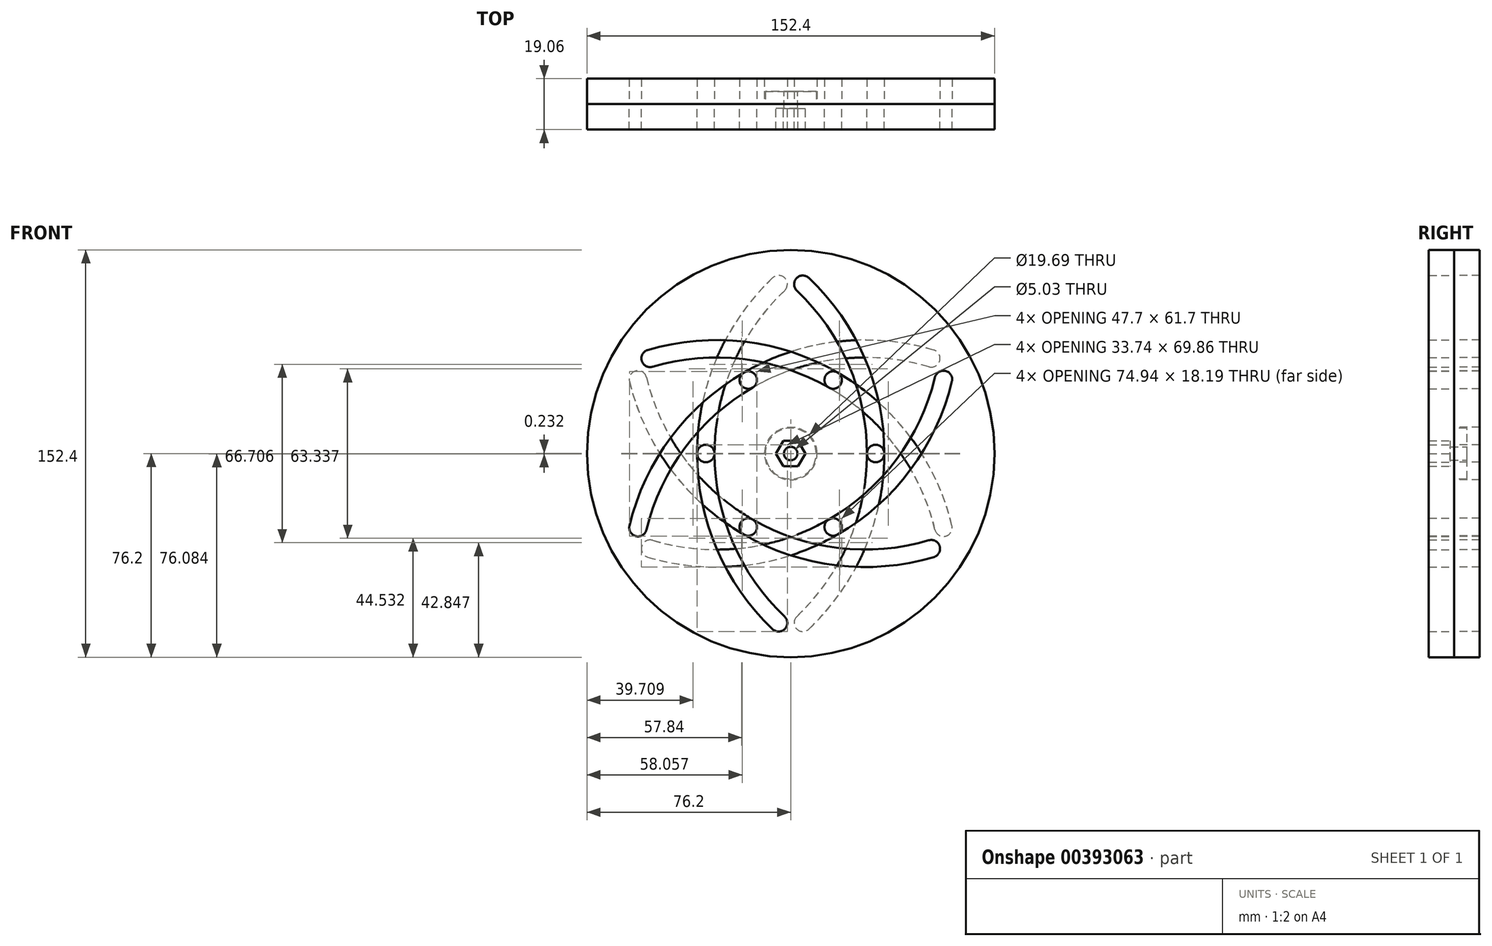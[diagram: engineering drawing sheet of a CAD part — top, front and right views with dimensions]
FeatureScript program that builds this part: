
annotation { "Feature Type Name" : "Feature", "Feature Type Description" : "" }
export const myFeature = defineFeature(function(context is Context, id is Id, definition is map)
    precondition{}
    {
        {
            var Q0;
            Q0=qCreatedBy(makeId("Front.planeOp"),FACE);
            var sketch = newSketch(context, id + "F0", { "sketchPlane" : qUnion([Q0])});
            skCircle(sketch, "E0", {"center": v(0, 0) * mm, "radius": 76.2 * mm});
            skLineSegment(sketch, "E1", {"start": v(38.1, -66) * mm, "end": v(-38.1, 66) * mm, "construction": true});
            skLineSegment(sketch, "E2", {"start": v(-76.2, 0) * mm, "end": v(76.2, 0) * mm, "construction": true});
            skCircle(sketch, "E3", {"center": v(0, 0) * mm, "radius": 63.5 * mm, "construction": true});
            skCircle(sketch, "E4", {"center": v(0, 0) * mm, "radius": 55.56 * mm, "construction": true});
            skCircle(sketch, "E5", {"center": v(0, 0) * mm, "radius": 31.75 * mm, "construction": true});
            skLineSegment(sketch, "E6", {"start": v(31.54, -3.6) * mm, "end": v(63.09, -7.22) * mm, "construction": true});
            skPoint(sketch, "E7", {"position": v(47.32, -5.41) * mm});
            skArc(sketch, "E8", {"start": v(57.12, 27.74) * mm, "mid": v(42.18, -4.12) * mm, "end": v(15.87, -27.5) * mm, "construction": true});
            skArc(sketch, "E9.0.startCap", {"start": v(53.95, 28.5) * mm, "mid": v(57.88, 30.91) * mm, "end": v(60.3, 26.98) * mm});
            skArc(sketch, "E9.0.endCap", {"start": v(17.5, -30.32) * mm, "mid": v(13.05, -29.13) * mm, "end": v(14.24, -24.67) * mm});
            skArc(sketch, "E9.0.left", {"start": v(60.3, 26.98) * mm, "mid": v(44.8, -6.07) * mm, "end": v(17.5, -30.32) * mm});
            skArc(sketch, "E9.0.right", {"start": v(53.95, 28.5) * mm, "mid": v(39.56, -2.17) * mm, "end": v(14.24, -24.67) * mm});
            skArc(sketch, "E10.1.0", {"start": v(6.78, 65.7) * mm, "mid": v(27.66, 35.76) * mm, "end": v(35.01, 0) * mm});
            skArc(sketch, "E10.1.1", {"start": v(35.01, 0) * mm, "mid": v(31.75, -3.26) * mm, "end": v(28.49, 0) * mm});
            skArc(sketch, "E10.1.2", {"start": v(2.29, 60.97) * mm, "mid": v(21.66, 33.18) * mm, "end": v(28.49, 0) * mm});
            skArc(sketch, "E10.1.3", {"start": v(2.29, 60.97) * mm, "mid": v(2.17, 65.58) * mm, "end": v(6.78, 65.7) * mm});
            skArc(sketch, "E10.2.0", {"start": v(-53.51, 38.73) * mm, "mid": v(-17.14, 41.83) * mm, "end": v(17.5, 30.32) * mm});
            skArc(sketch, "E10.2.1", {"start": v(17.5, 30.32) * mm, "mid": v(18.7, 25.86) * mm, "end": v(14.24, 24.67) * mm});
            skArc(sketch, "E10.2.2", {"start": v(-51.66, 32.47) * mm, "mid": v(-17.9, 35.35) * mm, "end": v(14.24, 24.67) * mm});
            skArc(sketch, "E10.2.3", {"start": v(-51.66, 32.47) * mm, "mid": v(-55.71, 34.67) * mm, "end": v(-53.51, 38.73) * mm});
            skArc(sketch, "E10.3.0", {"start": v(-60.3, -26.98) * mm, "mid": v(-44.8, 6.07) * mm, "end": v(-17.5, 30.32) * mm});
            skArc(sketch, "E10.3.1", {"start": v(-17.5, 30.32) * mm, "mid": v(-13.05, 29.13) * mm, "end": v(-14.24, 24.67) * mm});
            skArc(sketch, "E10.3.2", {"start": v(-53.95, -28.5) * mm, "mid": v(-39.56, 2.17) * mm, "end": v(-14.24, 24.67) * mm});
            skArc(sketch, "E10.3.3", {"start": v(-53.95, -28.5) * mm, "mid": v(-57.88, -30.91) * mm, "end": v(-60.3, -26.98) * mm});
            skArc(sketch, "E10.4.0", {"start": v(-6.78, -65.7) * mm, "mid": v(-27.66, -35.76) * mm, "end": v(-35.01, 0) * mm});
            skArc(sketch, "E10.4.1", {"start": v(-35.01, 0) * mm, "mid": v(-31.75, 3.26) * mm, "end": v(-28.49, 0) * mm});
            skArc(sketch, "E10.4.2", {"start": v(-2.29, -60.97) * mm, "mid": v(-21.66, -33.18) * mm, "end": v(-28.49, 0) * mm});
            skArc(sketch, "E10.4.3", {"start": v(-2.29, -60.97) * mm, "mid": v(-2.17, -65.58) * mm, "end": v(-6.78, -65.7) * mm});
            skArc(sketch, "E10.5.0", {"start": v(53.51, -38.73) * mm, "mid": v(17.14, -41.83) * mm, "end": v(-17.5, -30.32) * mm});
            skArc(sketch, "E10.5.1", {"start": v(-17.5, -30.32) * mm, "mid": v(-18.7, -25.86) * mm, "end": v(-14.24, -24.67) * mm});
            skArc(sketch, "E10.5.2", {"start": v(51.66, -32.47) * mm, "mid": v(17.9, -35.35) * mm, "end": v(-14.24, -24.67) * mm});
            skArc(sketch, "E10.5.3", {"start": v(51.66, -32.47) * mm, "mid": v(55.71, -34.67) * mm, "end": v(53.51, -38.73) * mm});
            skPoint(sketch, "E11", {"position": v(55.2, -6.31) * mm});
            skCircle(sketch, "E12.cCircle", {"center": v(0, 0) * mm, "radius": 4.76 * mm, "construction": true});
            skLineSegment(sketch, "E12.0", {"start": v(2.75, 4.76) * mm, "end": v(5.5, 0) * mm});
            skLineSegment(sketch, "E12.1", {"start": v(5.5, 0) * mm, "end": v(2.75, -4.76) * mm});
            skLineSegment(sketch, "E12.2", {"start": v(2.75, -4.76) * mm, "end": v(-2.75, -4.76) * mm});
            skLineSegment(sketch, "E12.3", {"start": v(-2.75, -4.76) * mm, "end": v(-5.5, 0) * mm});
            skLineSegment(sketch, "E12.4", {"start": v(-5.5, 0) * mm, "end": v(-2.75, 4.76) * mm});
            skLineSegment(sketch, "E12.5", {"start": v(-2.75, 4.76) * mm, "end": v(2.75, 4.76) * mm});
            skPoint(sketch, "E12.0.midPoint", {"position": v(4.12, 2.38) * mm});
            skCircle(sketch, "E13", {"center": v(0, 0) * mm, "radius": 2.51 * mm});
            skCircle(sketch, "E14", {"center": v(0, 0) * mm, "radius": 9.53 * mm});
            skLineSegment(sketch, "E15", {"start": v(0, 0) * mm, "end": v(0, 76.2) * mm, "construction": true});
            skCircle(sketch, "E16", {"center": v(0, 0) * mm, "radius": 9.84 * mm});
            skSolve(sketch);
        }
        {
            var Q0;
            Q0 = qSketchRegion(id + "F0", true);
            var Q1;
            Q1=makeQuery(id+"F0.imprint","IMPRINT",FACE,{"disambiguationData":[TD([[makeQuery(id+"F0.imprint","IMPRINT",EDGE,{"derivedFrom":sQuery(id+"F0.wireOp",EDGE,"E12.0")}),1.0]])]});
            var Q2;
            Q2=makeQuery(id+"F0.imprint","IMPRINT",FACE,{"disambiguationData":[TD([[makeQuery(id+"F0.imprint","IMPRINT",EDGE,{"derivedFrom":sQuery(id+"F0.wireOp",EDGE,"E14")}),-1.0]])]});
            extrude(context, id + "F1", {"entities" : qUnion([Q0, Q1, Q2]), "depth" : 9.52 * mm});
        }
        {
            var Q0;
            Q0=makeQuery(id+"F0.imprint","IMPRINT",FACE,{"disambiguationData":[TD([[makeQuery(id+"F0.imprint","IMPRINT",EDGE,{"derivedFrom":sQuery(id+"F0.wireOp",EDGE,"E12.0")}),-1.0]])]});
            extrude(context, id + "F2", {"entities" : qUnion([Q0]), "operationType" : NewBodyOperationType.ADD, "depth" : 1.59 * mm});
        }
        {
            var Q0;
            Q0=makeQuery(id+"F0.imprint","IMPRINT",FACE,{"disambiguationData":[TD([[makeQuery(id+"F0.imprint","IMPRINT",EDGE,{"derivedFrom":sQuery(id+"F0.wireOp",EDGE,"E12.0")}),1.0]])]});
            var Q1;
            Q1=makeQuery(id+"F0.imprint","IMPRINT",FACE,{"disambiguationData":[TD([[makeQuery(id+"F0.imprint","IMPRINT",EDGE,{"derivedFrom":sQuery(id+"F0.wireOp",EDGE,"E12.0")}),-1.0]])]});
            extrude(context, id + "F3", {"entities" : qUnion([Q0, Q1]), "operationType" : NewBodyOperationType.ADD, "oppositeDirection" : true, "depth" : 4.76 * mm});
        }
        {
            var Q0;
            Q0=makeQuery(id+"F0.imprint","IMPRINT",FACE,{"disambiguationData":[TD([[makeQuery(id+"F0.imprint","IMPRINT",EDGE,{"derivedFrom":sQuery(id+"F0.wireOp",EDGE,"E0")}),1.0]])]});
            var Q1;
            Q1=makeQuery(id+"F1.opExtrude","CAP_FACE",FACE,{"disambiguationData":[OSD([sQuery(id+"F0.wireOp",EDGE,"E0"),sQuery(id+"F0.wireOp",EDGE,"E9.0.startCap"),sQuery(id+"F0.wireOp",EDGE,"E9.0.endCap"),sQuery(id+"F0.wireOp",EDGE,"E9.0.left"),sQuery(id+"F0.wireOp",EDGE,"E9.0.right"),sQuery(id+"F0.wireOp",EDGE,"E10.1.0"),sQuery(id+"F0.wireOp",EDGE,"E10.1.1"),sQuery(id+"F0.wireOp",EDGE,"E10.1.2"),sQuery(id+"F0.wireOp",EDGE,"E10.1.3"),sQuery(id+"F0.wireOp",EDGE,"E10.2.0"),sQuery(id+"F0.wireOp",EDGE,"E10.2.1"),sQuery(id+"F0.wireOp",EDGE,"E10.2.2"),sQuery(id+"F0.wireOp",EDGE,"E10.2.3"),sQuery(id+"F0.wireOp",EDGE,"E10.3.0"),sQuery(id+"F0.wireOp",EDGE,"E10.3.1"),sQuery(id+"F0.wireOp",EDGE,"E10.3.2"),sQuery(id+"F0.wireOp",EDGE,"E10.3.3"),sQuery(id+"F0.wireOp",EDGE,"E10.4.0"),sQuery(id+"F0.wireOp",EDGE,"E10.4.1"),sQuery(id+"F0.wireOp",EDGE,"E10.4.2"),sQuery(id+"F0.wireOp",EDGE,"E10.4.3"),sQuery(id+"F0.wireOp",EDGE,"E10.5.0"),sQuery(id+"F0.wireOp",EDGE,"E10.5.1"),sQuery(id+"F0.wireOp",EDGE,"E10.5.2"),sQuery(id+"F0.wireOp",EDGE,"E10.5.3"),sQuery(id+"F0.wireOp",EDGE,"E12.0"),sQuery(id+"F0.wireOp",EDGE,"E12.1"),sQuery(id+"F0.wireOp",EDGE,"E12.2"),sQuery(id+"F0.wireOp",EDGE,"E12.3"),sQuery(id+"F0.wireOp",EDGE,"E12.4"),sQuery(id+"F0.wireOp",EDGE,"E12.5")])],"isStart":false});
            extrude(context, id + "F4", {"entities" : qUnion([Q0]), "endBound" : BoundingType.UP_TO_SURFACE, "endBoundEntityFace" : qUnion([Q1]), "depth" : 25.4 * mm});
        }
        {
            var Q0;
            Q0=makeQuery(id+"F4.opExtrude","SWEPT_BODY",BODY,{"disambiguationData":[OSD([sQuery(id+"F0.wireOp",EDGE,"E0"),sQuery(id+"F0.wireOp",EDGE,"E9.0.startCap"),sQuery(id+"F0.wireOp",EDGE,"E9.0.endCap"),sQuery(id+"F0.wireOp",EDGE,"E9.0.left"),sQuery(id+"F0.wireOp",EDGE,"E9.0.right"),sQuery(id+"F0.wireOp",EDGE,"E10.1.0"),sQuery(id+"F0.wireOp",EDGE,"E10.1.1"),sQuery(id+"F0.wireOp",EDGE,"E10.1.2"),sQuery(id+"F0.wireOp",EDGE,"E10.1.3"),sQuery(id+"F0.wireOp",EDGE,"E10.2.0"),sQuery(id+"F0.wireOp",EDGE,"E10.2.1"),sQuery(id+"F0.wireOp",EDGE,"E10.2.2"),sQuery(id+"F0.wireOp",EDGE,"E10.2.3"),sQuery(id+"F0.wireOp",EDGE,"E10.3.0"),sQuery(id+"F0.wireOp",EDGE,"E10.3.1"),sQuery(id+"F0.wireOp",EDGE,"E10.3.2"),sQuery(id+"F0.wireOp",EDGE,"E10.3.3"),sQuery(id+"F0.wireOp",EDGE,"E10.4.0"),sQuery(id+"F0.wireOp",EDGE,"E10.4.1"),sQuery(id+"F0.wireOp",EDGE,"E10.4.2"),sQuery(id+"F0.wireOp",EDGE,"E10.4.3"),sQuery(id+"F0.wireOp",EDGE,"E10.5.0"),sQuery(id+"F0.wireOp",EDGE,"E10.5.1"),sQuery(id+"F0.wireOp",EDGE,"E10.5.2"),sQuery(id+"F0.wireOp",EDGE,"E10.5.3"),sQuery(id+"F0.wireOp",EDGE,"E13")])]});
            var Q1;
            Q1=sQuery(id+"F0.wireOp",EDGE,"E15");
            transform(context, id + "F5", {"entities" : qUnion([Q0]), "transformType" : TransformType.ROTATION, "transformAxis" : qUnion([Q1]), "angle" : 180 * degree, "makeCopy" : false});
        }
    });
